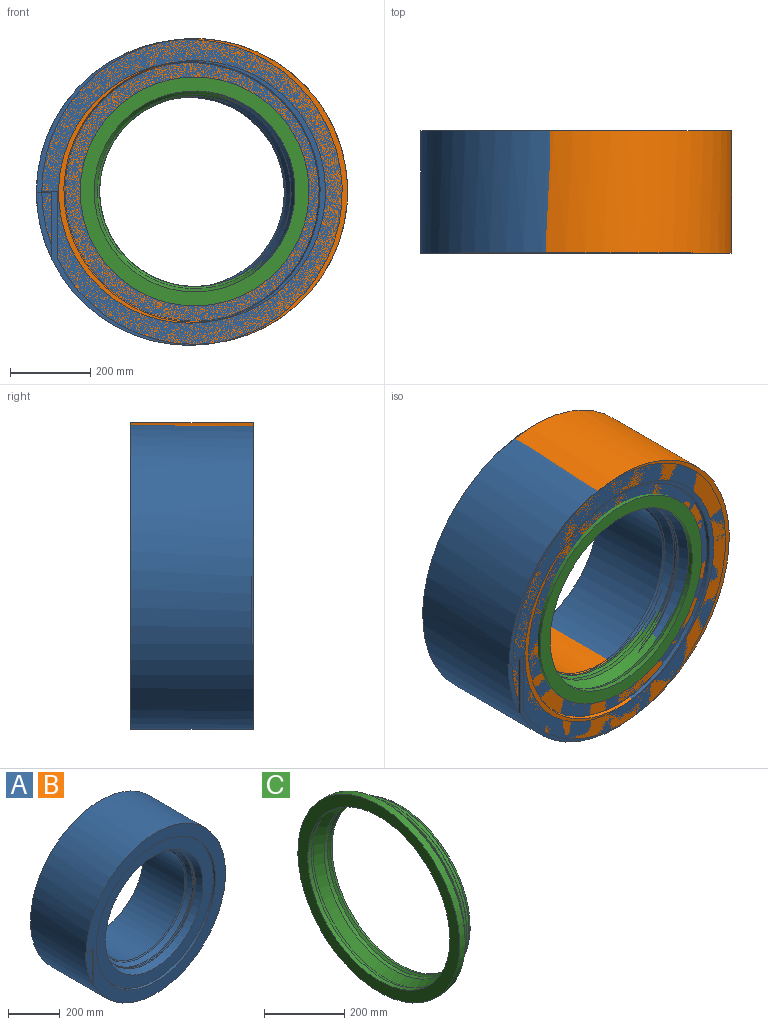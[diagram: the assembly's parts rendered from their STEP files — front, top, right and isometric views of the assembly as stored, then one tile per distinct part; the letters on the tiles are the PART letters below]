
ASSEMBLY  parts=3 mates=1
PART A: 15 faces, bbox 761.9x304.8x761.9 mm
  f0: cylinder r=236.54mm len=473.08mm, axis (0,-1,0), area 338206.6mm2, adj f2,f6
  f1: cylinder r=380.94mm len=761.87mm, axis (0,-1,0), area 728756.5mm2, adj f2,f3,f12,f13,f14
  f2: plane 761.87x761.87mm, normal (0,1,0), area 280112.7mm2, adj f0,f1
  f3: plane 761.87x761.87mm, normal (0,-1,0), area 117835.2mm2, adj f1,f5,f13,f14
  f4: plane 646.89x646.89mm, normal (0,-1,0), area 104713.3mm2, adj f5,f11
  f5: cone r=325.91mm half-angle=14.5deg, axis (0,-1,0), area 20070.3mm2, adj f3,f4
  f6: cone r=240.98mm half-angle=45deg, axis (0,-1,0), area 9420.3mm2, adj f0,f7
  f7: cone r=252.58mm half-angle=30deg, axis (0,-1,0), area 35972.1mm2, adj f6,f8
  f8: cylinder r=252.58mm len=505.16mm, axis (0,1,0), area 11532.2mm2, adj f7,f9
  f9: cone r=254.36mm half-angle=23deg, axis (0,-1,0), area 7246.9mm2, adj f8,f10
  f10: cylinder r=254.36mm len=508.71mm, axis (0,1,0), area 3124.2mm2, adj f9,f11
  f11: cone r=266.99mm half-angle=23deg, axis (0,-1,0), area 52969.5mm2, adj f4,f10
  f12: plane 167.31x38.71mm, normal (0,-1,0), area 4363.3mm2, adj f1,f13,f14
  f13: plane 167.31x4.51mm, normal (-1,0,0), area 754mm2, adj f1,f3,f12,f14
  f14: plane 38.71x4.51mm, normal (0,0,-1), area 174.5mm2, adj f1,f3,f12,f13
PART B: same geometry as A
PART C: 24 faces, bbox 121x596x596 mm
  f0: cone r=253.95mm half-angle=67deg, axis (1,0,0), area 6121.2mm2, adj f1,f23
  f1: cone r=258.41mm half-angle=23deg, axis (-1,0,0), area 18398.2mm2, adj f0,f2
  f2: cone r=261.92mm half-angle=67deg, axis (1,0,0), area 6228.2mm2, adj f1,f3
  f3: cone r=263.19mm half-angle=23deg, axis (-1,0,0), area 5371.5mm2, adj f2,f4
  f4: torus R=148.32mm, axis (-1,0,0), area 15188mm2, adj f3,f5
  f5: cone r=266.78mm half-angle=45deg, axis (1,0,0), area 1505.3mm2, adj f4,f6
  f6: torus R=266.35mm, axis (-1,0,0), area 373.7mm2, adj f5,f7
  f7: cylinder r=266.06mm len=532.13mm, axis (-1,0,0), area 3050.5mm2, adj f6,f8
  f8: torus R=266.35mm, axis (-1,0,0), area 747.7mm2, adj f7,f9
  f9: plane 569.6x569.6mm, normal (1,0,0), area 31950.3mm2, adj f8,f10
  f10: cone r=285.19mm half-angle=1.1deg, axis (-1,0,0), area 35050.5mm2, adj f9,f11
  f11: plane 570.38x570.38mm, normal (-1,0,0), area 58498.9mm2, adj f10,f12
  f12: cylinder r=250.42mm len=500.85mm, axis (-1,0,0), area 20031.7mm2, adj f11,f13
  f13: cone r=255.32mm half-angle=24.4deg, axis (1,0,0), area 18800.8mm2, adj f12,f14
  f14: cone r=242.57mm half-angle=25.7deg, axis (-1,0,0), area 46063.5mm2, adj f13,f15
  f15: cylinder r=242.57mm len=485.14mm, axis (-1,0,0), area 17236.2mm2, adj f14,f16
  f16: cone r=237.1mm half-angle=45deg, axis (-1,0,0), area 11647.4mm2, adj f15,f17
  f17: cone r=237.1mm half-angle=15deg, axis (1,0,0), area 11391.9mm2, adj f16,f18
  f18: plane 494.93x494.93mm, normal (1,0,0), area 12825.4mm2, adj f17,f19
  f19: torus R=139.32mm, axis (-1,0,0), area 14306.8mm2, adj f18,f20
  f20: torus R=249.94mm, axis (-1,0,0), area 1738.7mm2, adj f19,f21
  f21: cylinder r=252.22mm len=504.44mm, axis (-1,0,0), area 12652.1mm2, adj f20,f22
  f22: torus R=254.51mm, axis (-1,0,0), area 1454.6mm2, adj f21,f23
  f23: cone r=257.46mm half-angle=23deg, axis (-1,0,0), area 20711.3mm2, adj f0,f22
PLACE A t=(77.52,92.44,57.72)mm
PLACE B t=(90.76,92.44,60.06)mm
PLACE C rot(axis=(-0.58,-0.58,0.58),120deg) t=(90.76,166.62,60.06)mm
MATE cylindrical C.f0 <-> A.f3  axis (0,-1,0) through (90.76,92.44,60.06)mm
